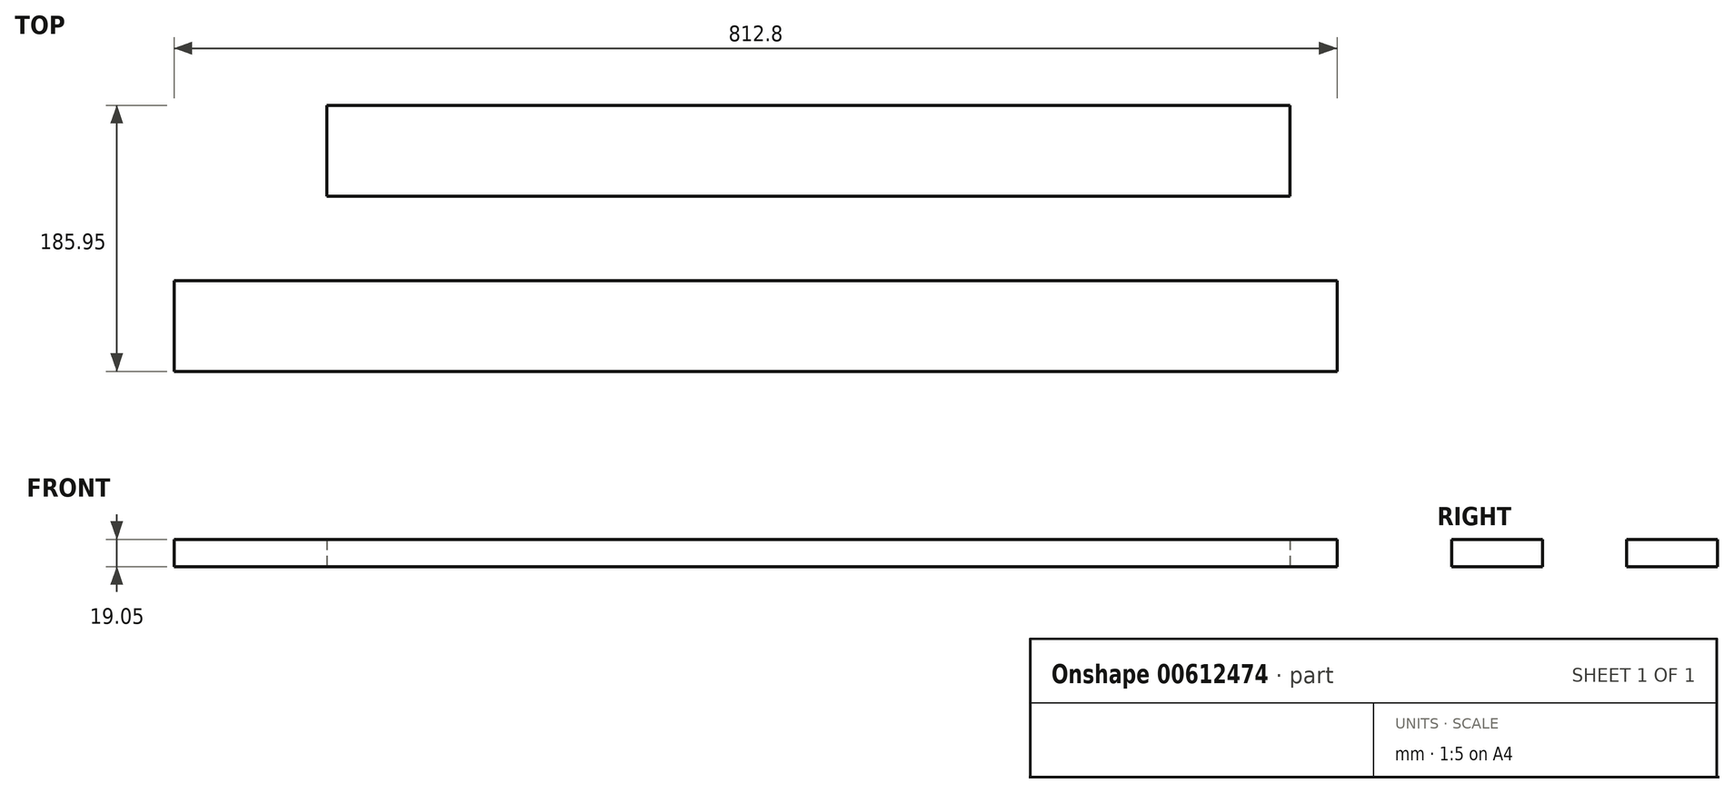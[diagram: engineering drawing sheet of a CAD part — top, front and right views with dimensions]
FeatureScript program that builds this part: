
annotation { "Feature Type Name" : "Feature", "Feature Type Description" : "" }
export const myFeature = defineFeature(function(context is Context, id is Id, definition is map)
    precondition{}
    {
        {
            var Q0;
            Q0=qCreatedBy(makeId("Top.planeOp"),FACE);
            var sketch = newSketch(context, id + "F0", { "sketchPlane" : qUnion([Q0])});
            skLineSegment(sketch, "E0.bottom", {"start": v(-315.4, 60.65) * mm, "end": v(357.7, 60.65) * mm});
            skLineSegment(sketch, "E0.top", {"start": v(-315.4, -2.85) * mm, "end": v(357.7, -2.85) * mm});
            skLineSegment(sketch, "E0.left", {"start": v(-315.4, 60.65) * mm, "end": v(-315.4, -2.85) * mm});
            skLineSegment(sketch, "E0.right", {"start": v(357.7, 60.65) * mm, "end": v(357.7, -2.85) * mm});
            skLineSegment(sketch, "E1.bottom", {"start": v(-422.24, -61.8) * mm, "end": v(390.56, -61.8) * mm});
            skLineSegment(sketch, "E1.top", {"start": v(-422.24, -125.3) * mm, "end": v(390.56, -125.3) * mm});
            skLineSegment(sketch, "E1.left", {"start": v(-422.24, -61.8) * mm, "end": v(-422.24, -125.3) * mm});
            skLineSegment(sketch, "E1.right", {"start": v(390.56, -61.8) * mm, "end": v(390.56, -125.3) * mm});
            skSolve(sketch);
        }
        {
            var Q0;
            Q0=makeQuery(id+"F0.imprint","IMPRINT",FACE,{"disambiguationData":[TD([[makeQuery(id+"F0.imprint","IMPRINT",EDGE,{"derivedFrom":sQuery(id+"F0.wireOp",EDGE,"E0.bottom")}),-1.0]])]});
            var Q1;
            Q1=makeQuery(id+"F0.imprint","IMPRINT",FACE,{"disambiguationData":[TD([[makeQuery(id+"F0.imprint","IMPRINT",EDGE,{"derivedFrom":sQuery(id+"F0.wireOp",EDGE,"E1.bottom")}),-1.0]])]});
            extrude(context, id + "F1", {"entities" : qUnion([Q0, Q1]), "depth" : 19.05 * mm, "offsetDistance" : 25.4 * mm});
        }
    });
